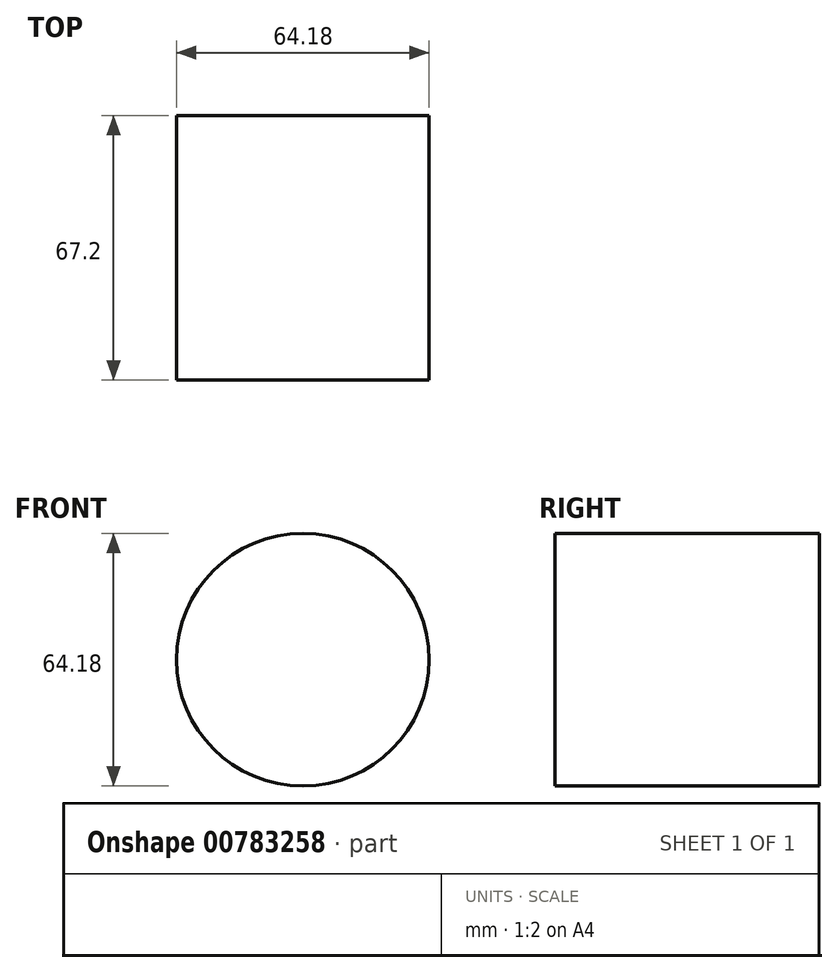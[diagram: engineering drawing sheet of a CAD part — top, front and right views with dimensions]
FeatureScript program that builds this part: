
annotation { "Feature Type Name" : "Feature", "Feature Type Description" : "" }
export const myFeature = defineFeature(function(context is Context, id is Id, definition is map)
    precondition{}
    {
        {
            var Q0;
            Q0=qCreatedBy(makeId("Front.planeOp"),FACE);
            var sketch = newSketch(context, id + "F0", { "sketchPlane" : qUnion([Q0])});
            skCircle(sketch, "E0", {"center": v(0, 0) * mm, "radius": 32.09 * mm});
            skSolve(sketch);
        }
        {
            var Q0;
            Q0=makeQuery(id+"F0.imprint","IMPRINT",FACE,{"disambiguationData":[TD([[makeQuery(id+"F0.imprint","IMPRINT",EDGE,{"derivedFrom":sQuery(id+"F0.wireOp",EDGE,"E0")}),1.0]])]});
            extrude(context, id + "F1", {"entities" : qUnion([Q0]), "depth" : 67.2 * mm, "offsetDistance" : 25 * mm});
        }
    });
